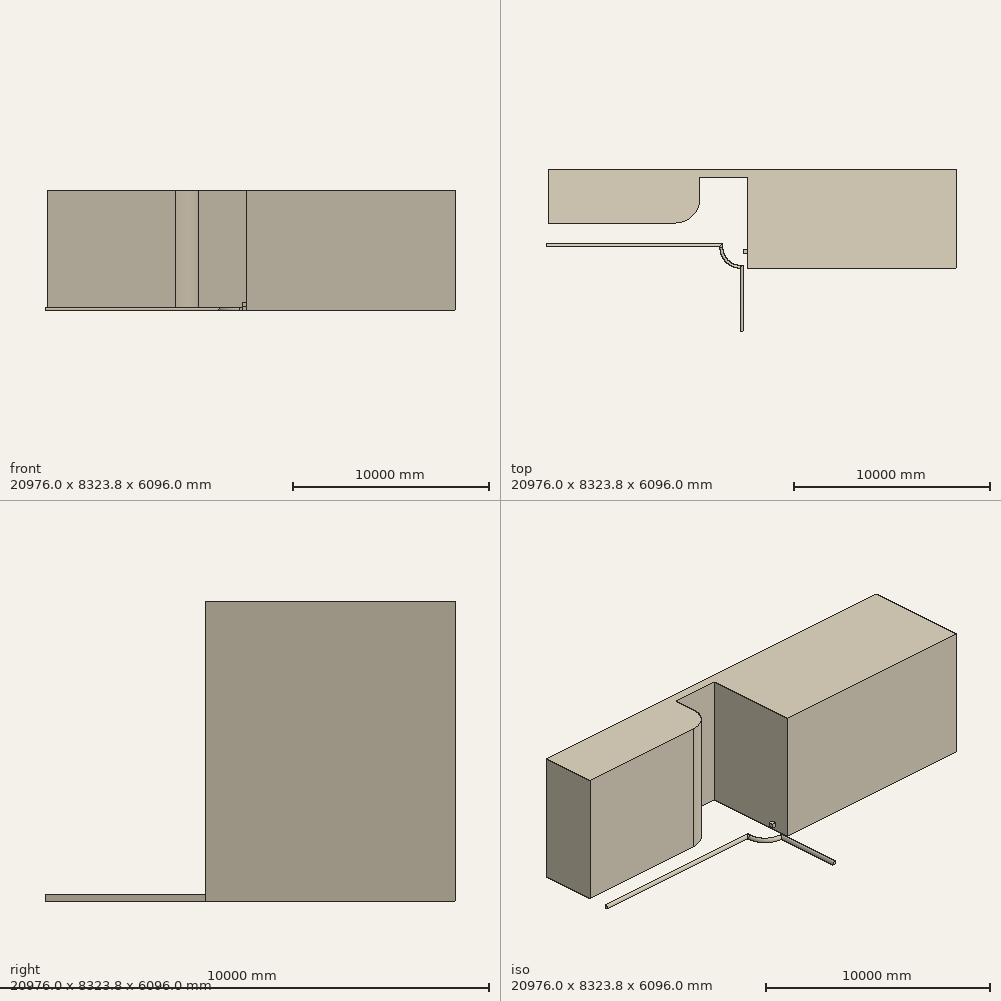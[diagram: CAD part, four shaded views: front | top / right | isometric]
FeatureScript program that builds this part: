
annotation { "Feature Type Name" : "Feature", "Feature Type Description" : "" }
export const myFeature = defineFeature(function(context is Context, id is Id, definition is map)
    precondition{}
    {
        {
            var Q0;
            Q0=qCreatedBy(makeId("Top.planeOp"),FACE);
            var sketch = newSketch(context, id + "F9", { "sketchPlane" : qUnion([Q0])});
            skLineSegment(sketch, "E0", {"start": v(-7759.81, 0) * mm, "end": v(0, 0) * mm});
            skLineSegment(sketch, "E1", {"start": v(0, 2308.06) * mm, "end": v(2438.4, 2308.06) * mm});
            skLineSegment(sketch, "E2", {"start": v(2438.4, 2308.06) * mm, "end": v(2438.4, -2310.78) * mm});
            skLineSegment(sketch, "E3", {"start": v(2438.4, -2310.78) * mm, "end": v(13126.7, -2310.78) * mm});
            skLineSegment(sketch, "E4", {"start": v(0, 2308.06) * mm, "end": v(0, 0) * mm});
            skLineSegment(sketch, "E5", {"start": v(-7849.32, -1044.65) * mm, "end": v(1180.88, -1044.65) * mm});
            skLineSegment(sketch, "E6", {"start": v(1180.88, -1044.65) * mm, "end": v(1180.88, -1244.17) * mm});
            skLineSegment(sketch, "E7", {"start": v(2095.28, -2158.57) * mm, "end": v(2221.43, -2158.57) * mm});
            skLineSegment(sketch, "E8", {"start": v(2221.43, -2158.57) * mm, "end": v(2221.43, -5567.8) * mm});
            skLineSegment(sketch, "E9", {"start": v(-7759.81, 0) * mm, "end": v(-7759.81, 2756) * mm});
            skLineSegment(sketch, "E10", {"start": v(-7759.81, 2756) * mm, "end": v(13126.7, 2756) * mm});
            skLineSegment(sketch, "E11", {"start": v(13126.7, 2756) * mm, "end": v(13126.7, -2310.78) * mm});
            skPoint(sketch, "E12.visualSharp", {"position": v(1180.88, -2158.57) * mm});
            skArc(sketch, "E12.filletArc", {"start": v(1180.88, -1244.17) * mm, "mid": v(1448.7, -1890.75) * mm, "end": v(2095.28, -2158.57) * mm});
            skLineSegment(sketch, "E13", {"start": v(-88.68, 386.49) * mm, "end": v(2311.87, 386.49) * mm});
            skSolve(sketch);
        }
        {
            var Q0;
            Q0=makeQuery(id+"F9.imprint","IMPRINT",FACE,{"disambiguationData":[TD([[makeQuery(id+"F9.imprint","IMPRINT",EDGE,{"derivedFrom":sQuery(id+"F9.wireOp",EDGE,"E0")}),1.0]])]});
            extrude(context, id + "F0", {"entities" : qUnion([Q0]), "depth" : 6096 * mm});
        }
        {
            var Q0;
            Q0=sQuery(id+"F9.wireOp",VERTEX,"E5.start");
            var Q1;
            Q1=sQuery(id+"F9.wireOp",EDGE,"E5");
            cPlane(context, id + "F1", {"entities" : qUnion([Q0, Q1]), "cplaneType" : CPlaneType.LINE_POINT, "offset" : 25 * mm, "width" : 150 * mm, "height" : 150 * mm});
        }
        {
            var Q0;
            Q0=qCreatedBy(id+"F1.planeOp",FACE);
            var sketch = newSketch(context, id + "F2", { "sketchPlane" : qUnion([Q0])});
            skLineSegment(sketch, "E14", {"start": v(-1054.93, 0) * mm, "end": v(-1054.93, 149.56) * mm});
            skLineSegment(sketch, "E15", {"start": v(-1054.93, 0) * mm, "end": v(-1204.49, 0) * mm});
            skArc(sketch, "E16", {"start": v(-1054.93, 149.56) * mm, "mid": v(-1160.68, 105.76) * mm, "end": v(-1204.49, 0) * mm});
            skSolve(sketch);
        }
        {
            var Q0;
            Q0=qSketchRegion(id+"F2",true);
            var Q1;
            Q1=qConstructionFilter(qBodyType(qCreatedBy(id+"F2",EDGE),BodyType.WIRE),ConstructionObject.NO);
            var Q2;
            Q2=sQuery(id+"F9.wireOp",EDGE,"E5");
            var Q3;
            Q3=sQuery(id+"F9.wireOp",EDGE,"E6");
            var Q4;
            Q4=sQuery(id+"F9.wireOp",EDGE,"E12.filletArc");
            var Q5;
            Q5=sQuery(id+"F9.wireOp",EDGE,"E7");
            var Q6;
            Q6=sQuery(id+"F9.wireOp",EDGE,"E8");
            sweep(context, id + "F3", {"profiles" : qUnion([Q0]), "surfaceProfiles" : qUnion([Q1]), "path" : qUnion([Q2, Q3, Q4, Q5, Q6])});
        }
        {
            var Q0;
            Q0=makeQuery(id+"F0.opExtrude","SWEPT_FACE",FACE,{"disambiguationData":[OSD([sQuery(id+"F9.wireOp",EDGE,"E2")])]});
            var sketch = newSketch(context, id + "F4", { "sketchPlane" : qUnion([Q0])});
            skCircle(sketch, "E17", {"center": v(1460.93, 297.76) * mm, "radius": 25.4 * mm});
            skLineSegment(sketch, "E18.bottom", {"start": v(1573.22, 393.7) * mm, "end": v(1348.64, 393.7) * mm});
            skLineSegment(sketch, "E18.top", {"start": v(1573.22, 201.82) * mm, "end": v(1348.64, 201.82) * mm});
            skLineSegment(sketch, "E18.left", {"start": v(1573.22, 393.7) * mm, "end": v(1573.22, 201.82) * mm});
            skLineSegment(sketch, "E18.right", {"start": v(1348.64, 393.7) * mm, "end": v(1348.64, 201.82) * mm});
            skSolve(sketch);
        }
        {
            var Q0;
            Q0=makeQuery(id+"F4.imprint","IMPRINT",FACE,{"disambiguationData":[TD([[makeQuery(id+"F4.imprint","IMPRINT",EDGE,{"derivedFrom":sQuery(id+"F4.wireOp",EDGE,"E17")}),1.0]])]});
            extrude(context, id + "F5", {"entities" : qUnion([Q0]), "depth" : 101.6 * mm});
        }
        {
            var Q0;
            Q0=makeQuery(id+"F0.opExtrude","SWEPT_EDGE",EDGE,{"disambiguationData":[OSD([sQuery(id+"F9.wireOp",EDGE,"E0"),sQuery(id+"F9.wireOp",EDGE,"E4")])]});
            fillet(context, id + "F6", {"entities" : qUnion([Q0]), "radius" : 1219.2 * mm, "tangentPropagation" : true, "allowEdgeOverflow" : false});
        }
        {
            var Q0;
            Q0=sQuery(id+"F9.wireOp",EDGE,"E13");
            extrude(context, id + "F7", {"bodyType" : ToolBodyType.SURFACE, "surfaceEntities" : qUnion([Q0]), "depth" : 1828.8 * mm});
        }
        {
            var Q0;
            Q0=makeQuery(id+"F4.imprint","IMPRINT",FACE,{"disambiguationData":[TD([[makeQuery(id+"F4.imprint","IMPRINT",EDGE,{"derivedFrom":sQuery(id+"F4.wireOp",EDGE,"E17")}),1.0]])]});
            var Q1;
            Q1=makeQuery(id+"F4.imprint","IMPRINT",FACE,{"disambiguationData":[TD([[makeQuery(id+"F4.imprint","IMPRINT",EDGE,{"derivedFrom":sQuery(id+"F4.wireOp",EDGE,"E17")}),-1.0]])]});
            extrude(context, id + "F8", {"entities" : qUnion([Q0, Q1]), "depth" : 203.2 * mm});
        }
    });
